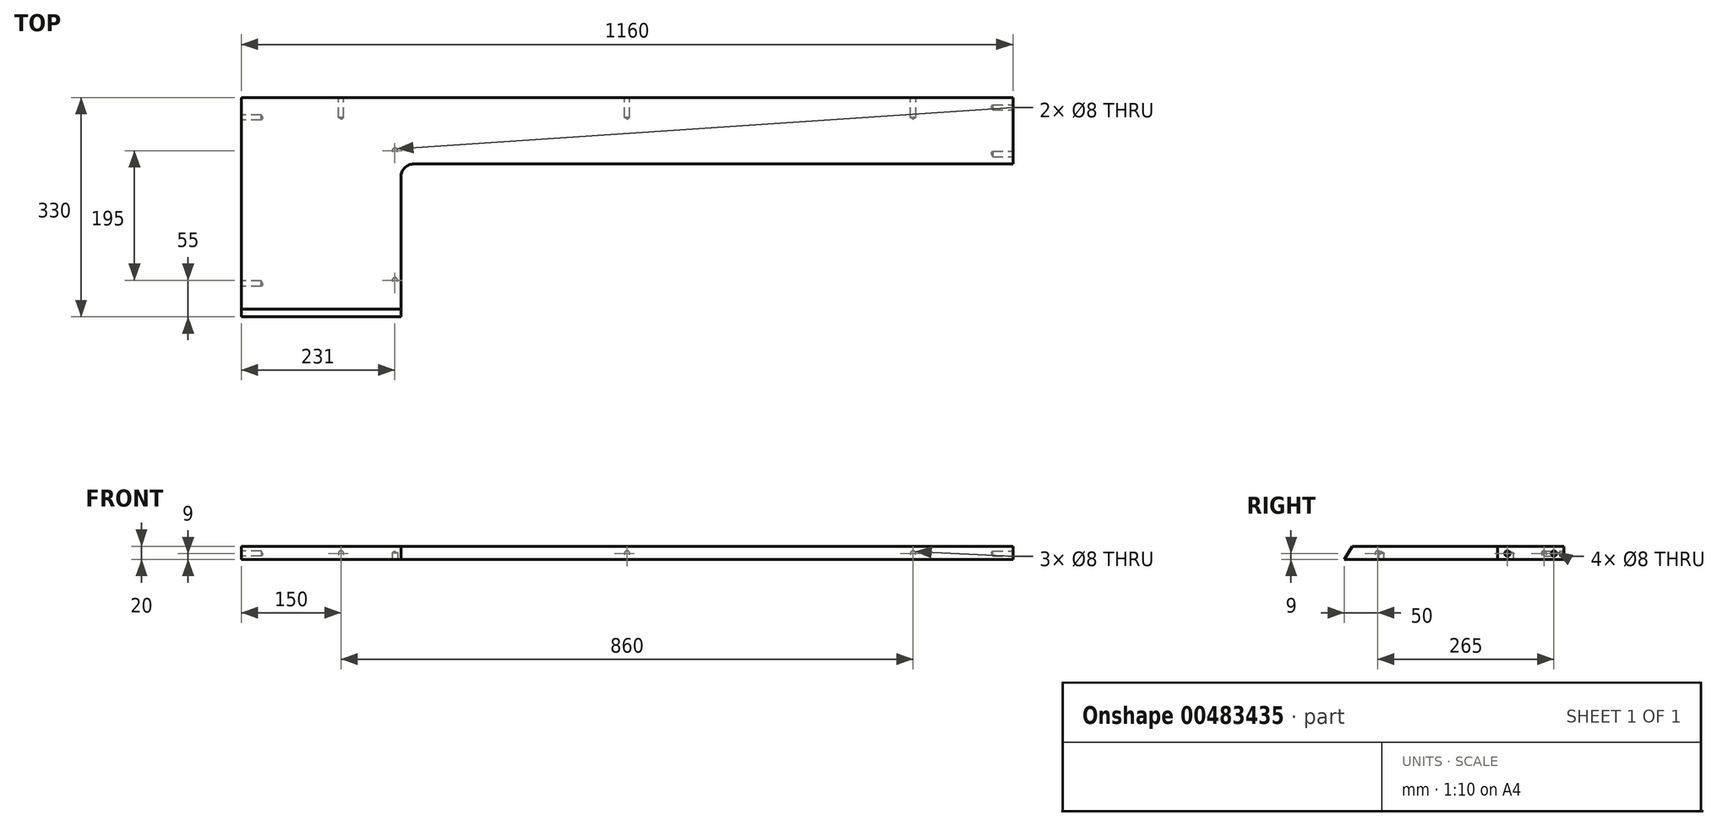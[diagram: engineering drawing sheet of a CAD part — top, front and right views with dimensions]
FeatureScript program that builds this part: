
annotation { "Feature Type Name" : "Feature", "Feature Type Description" : "" }
export const myFeature = defineFeature(function(context is Context, id is Id, definition is map)
    precondition{}
    {
        {
            var Q0;
            Q0=qCreatedBy(makeId("Top.planeOp"),FACE);
            var sketch = newSketch(context, id + "F0", { "sketchPlane" : qUnion([Q0])});
            skLineSegment(sketch, "E0.bottom", {"start": v(580, -165) * mm, "end": v(-580, -165) * mm});
            skLineSegment(sketch, "E0.top", {"start": v(580, 165) * mm, "end": v(-580, 165) * mm});
            skLineSegment(sketch, "E0.left", {"start": v(580, -165) * mm, "end": v(580, 165) * mm});
            skLineSegment(sketch, "E0.right", {"start": v(-580, -165) * mm, "end": v(-580, 165) * mm});
            skPoint(sketch, "E0.middle", {"position": v(0, 0) * mm});
            skSolve(sketch);
        }
        {
            var Q0;
            Q0=qSketchRegion(id+"F0",true);
            extrude(context, id + "F1", {"entities" : qUnion([Q0]), "depth" : 20 * mm});
        }
        {
            var Q0;
            Q0=makeQuery(id+"F1.opExtrude","CAP_FACE",FACE,{"disambiguationData":[OSD([sQuery(id+"F0.wireOp",EDGE,"E0.bottom"),sQuery(id+"F0.wireOp",EDGE,"E0.top"),sQuery(id+"F0.wireOp",EDGE,"E0.left"),sQuery(id+"F0.wireOp",EDGE,"E0.right")])],"isStart":false});
            var sketch = newSketch(context, id + "F2", { "sketchPlane" : qUnion([Q0])});
            skLineSegment(sketch, "E1.bottom", {"start": v(-340, -165) * mm, "end": v(580, -165) * mm});
            skLineSegment(sketch, "E1.top", {"start": v(-320, 65) * mm, "end": v(580, 65) * mm});
            skLineSegment(sketch, "E1.left", {"start": v(-340, -165) * mm, "end": v(-340, 45) * mm});
            skLineSegment(sketch, "E1.right", {"start": v(580, -165) * mm, "end": v(580, 65) * mm});
            skPoint(sketch, "E2.visualSharp", {"position": v(-340, 65) * mm});
            skArc(sketch, "E2.filletArc", {"start": v(-320, 65) * mm, "mid": v(-334.14, 59.14) * mm, "end": v(-340, 45) * mm});
            skPoint(sketch, "E3.visualSharp", {"position": v(580, 65) * mm});
            skSolve(sketch);
        }
        {
            var Q0;
            Q0=makeQuery(id+"F2.imprint","IMPRINT",FACE,{"disambiguationData":[TD([[makeQuery(id+"F2.imprint","IMPRINT",EDGE,{"derivedFrom":sQuery(id+"F2.wireOp",EDGE,"E1.bottom")}),-1.0]])]});
            extrude(context, id + "F3", {"entities" : qUnion([Q0]), "operationType" : NewBodyOperationType.REMOVE, "endBound" : BoundingType.THROUGH_ALL, "oppositeDirection" : true, "depth" : 25 * mm});
        }
        {
            var Q0;
            Q0=qCreatedBy(makeId("Right.planeOp"),FACE);
            var sketch = newSketch(context, id + "F4", { "sketchPlane" : qUnion([Q0])});
            skLineSegment(sketch, "E4", {"start": v(-165, 0) * mm, "end": v(-153.45, 20) * mm});
            skLineSegment(sketch, "E5", {"start": v(-153.45, 20) * mm, "end": v(-165, 20) * mm});
            skLineSegment(sketch, "E6", {"start": v(-165, 20) * mm, "end": v(-165, 0) * mm});
            skSolve(sketch);
        }
        {
            var Q0;
            Q0=makeQuery(id+"F4.imprint","IMPRINT",FACE,{"disambiguationData":[TD([[makeQuery(id+"F4.imprint","IMPRINT",EDGE,{"derivedFrom":sQuery(id+"F4.wireOp",EDGE,"E4")}),1.0]])]});
            extrude(context, id + "F5", {"entities" : qUnion([Q0]), "operationType" : NewBodyOperationType.REMOVE, "endBound" : BoundingType.THROUGH_ALL, "oppositeDirection" : true, "depth" : 25 * mm});
        }
        {
            var Q0;
            Q0=makeQuery(id+"F1.opExtrude","SWEPT_FACE",FACE,{"disambiguationData":[OSD([sQuery(id+"F0.wireOp",EDGE,"E0.right")])]});
            var sketch = newSketch(context, id + "F6", { "sketchPlane" : qUnion([Q0])});
            skPoint(sketch, "E7", {"position": v(-135, 9) * mm});
            skPoint(sketch, "E8", {"position": v(115, 9) * mm});
            skSolve(sketch);
        }
        {
            var Q0;
            Q0=makeQuery(id+"F1.opExtrude","SWEPT_FACE",FACE,{"disambiguationData":[OSD([sQuery(id+"F0.wireOp",EDGE,"E0.top")])]});
            var sketch = newSketch(context, id + "F7", { "sketchPlane" : qUnion([Q0])});
            skPoint(sketch, "E9", {"position": v(430, 9) * mm});
            skPoint(sketch, "E10", {"position": v(-430, 9) * mm});
            skPoint(sketch, "E11", {"position": v(0, 9) * mm});
            skSolve(sketch);
        }
        {
            var Q0;
            Q0=makeQuery(id+"F1.opExtrude","SWEPT_FACE",FACE,{"disambiguationData":[OSD([sQuery(id+"F0.wireOp",EDGE,"E0.left")])]});
            var sketch = newSketch(context, id + "F8", { "sketchPlane" : qUnion([Q0])});
            skPoint(sketch, "E12", {"position": v(80, 9) * mm});
            skPoint(sketch, "E13", {"position": v(150, 9) * mm});
            skSolve(sketch);
        }
        {
            var Q0;
            Q0=makeQuery(id+"F1.opExtrude","CAP_FACE",FACE,{"disambiguationData":[OSD([sQuery(id+"F0.wireOp",EDGE,"E0.bottom"),sQuery(id+"F0.wireOp",EDGE,"E0.top"),sQuery(id+"F0.wireOp",EDGE,"E0.left"),sQuery(id+"F0.wireOp",EDGE,"E0.right")])],"isStart":true});
            var sketch = newSketch(context, id + "F9", { "sketchPlane" : qUnion([Q0])});
            skPoint(sketch, "E14", {"position": v(-349, -85) * mm});
            skPoint(sketch, "E15", {"position": v(-349, 110) * mm});
            skSolve(sketch);
        }
        {
            var Q0;
            Q0=sQuery(id+"F6.wireOp",VERTEX,"E7");
            var Q1;
            Q1=sQuery(id+"F6.wireOp",VERTEX,"E8");
            var Q2;
            Q2=sQuery(id+"F7.wireOp",VERTEX,"E10");
            var Q3;
            Q3=sQuery(id+"F7.wireOp",VERTEX,"E11");
            var Q4;
            Q4=sQuery(id+"F7.wireOp",VERTEX,"E9");
            var Q5;
            Q5=sQuery(id+"F8.wireOp",VERTEX,"E12");
            var Q6;
            Q6=sQuery(id+"F8.wireOp",VERTEX,"E13");
            var Q7;
            Q7=makeQuery(id+"F1.opExtrude","SWEPT_BODY",BODY,{"disambiguationData":[OSD([sQuery(id+"F0.wireOp",EDGE,"E0.bottom"),sQuery(id+"F0.wireOp",EDGE,"E0.top"),sQuery(id+"F0.wireOp",EDGE,"E0.left"),sQuery(id+"F0.wireOp",EDGE,"E0.right")])]});
            hole(context, id + "F10", {"style" : HoleStyle.SIMPLE, "endStyle" : HoleEndStyle.BLIND, "standardTappedOrClearance" : lookupTablePath({ "standard" : "ISO", "size" : "8", "type" : "Drilled" }), "standardBlindInLast" : lookupTablePath({ "standard" : "ISO", "size" : "8", "type" : "Drilled" }), "holeDiameter" : 8 * mm, "holeDepth" : 30 * mm, "isTappedThrough" : true, "tappedDepth" : 12 * mm, "tapClearance" : 3, "locations" : qUnion([Q0, Q1, Q2, Q3, Q4, Q5, Q6]), "scope" : qUnion([Q7])});
        }
        {
            var Q0;
            Q0=sQuery(id+"F9.wireOp",VERTEX,"E14");
            var Q1;
            Q1=sQuery(id+"F9.wireOp",VERTEX,"E15");
            var Q2;
            Q2=makeQuery(id+"F1.opExtrude","SWEPT_BODY",BODY,{"disambiguationData":[OSD([sQuery(id+"F0.wireOp",EDGE,"E0.bottom"),sQuery(id+"F0.wireOp",EDGE,"E0.top"),sQuery(id+"F0.wireOp",EDGE,"E0.left"),sQuery(id+"F0.wireOp",EDGE,"E0.right")])]});
            hole(context, id + "F11", {"style" : HoleStyle.SIMPLE, "endStyle" : HoleEndStyle.BLIND, "standardTappedOrClearance" : lookupTablePath({ "standard" : "ISO", "size" : "8", "type" : "Drilled" }), "standardBlindInLast" : lookupTablePath({ "standard" : "ISO", "size" : "8", "type" : "Drilled" }), "holeDiameter" : 8 * mm, "holeDepth" : 10 * mm, "isTappedThrough" : true, "tappedDepth" : 12 * mm, "tapClearance" : 3, "locations" : qUnion([Q0, Q1]), "scope" : qUnion([Q2])});
        }
    });
